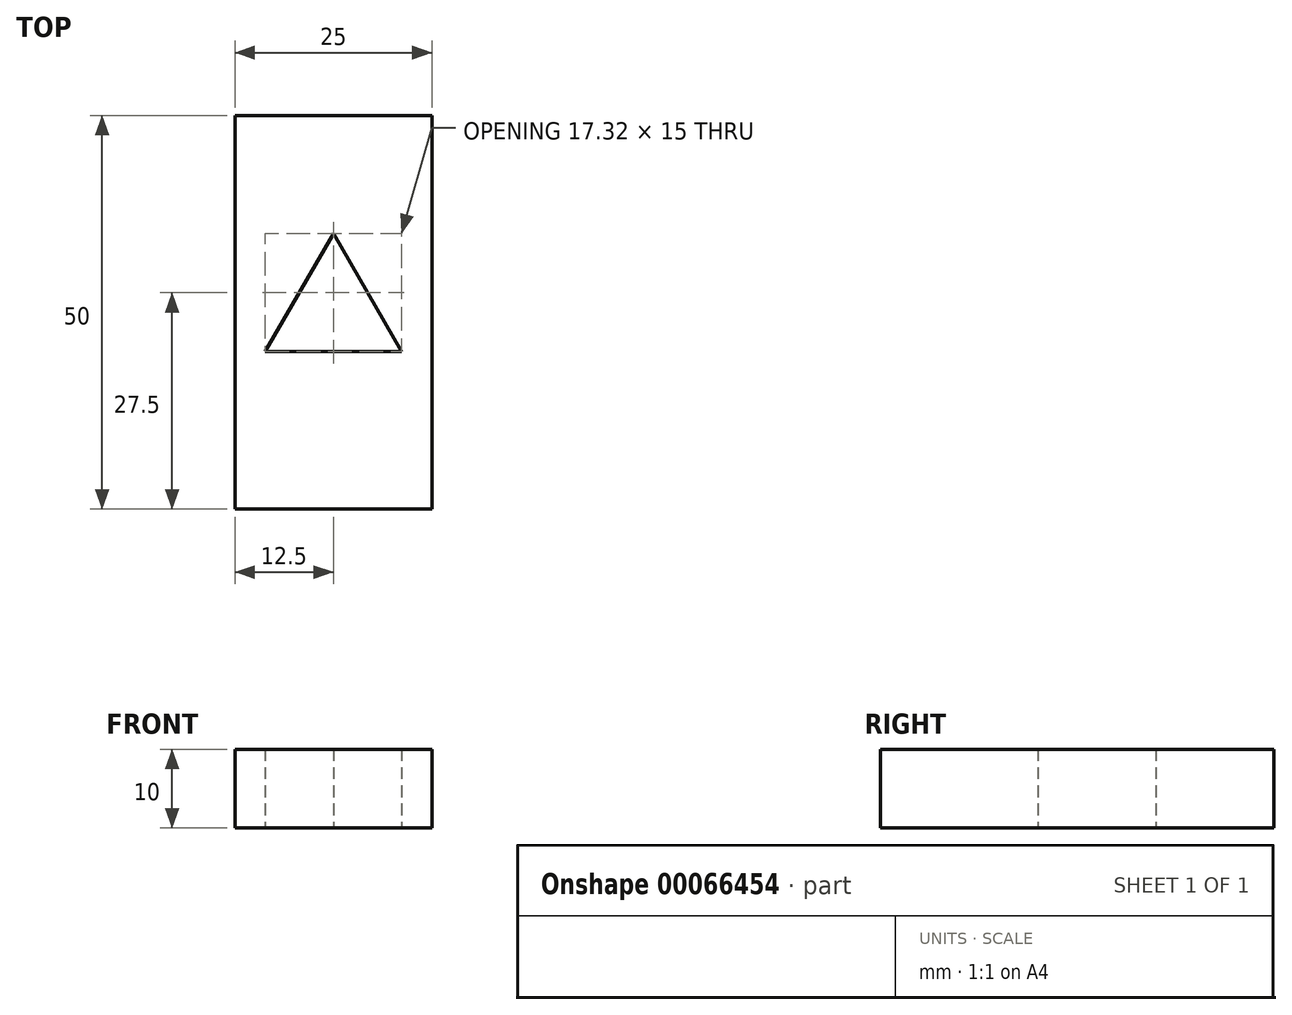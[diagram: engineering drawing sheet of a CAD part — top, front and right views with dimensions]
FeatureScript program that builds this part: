
annotation { "Feature Type Name" : "Feature", "Feature Type Description" : "" }
export const myFeature = defineFeature(function(context is Context, id is Id, definition is map)
    precondition{}
    {
        {
            var Q0;
            Q0=qCreatedBy(makeId("Top.planeOp"),FACE);
            var sketch = newSketch(context, id + "F0", { "sketchPlane" : qUnion([Q0])});
            skLineSegment(sketch, "E0.rect.bottom", {"start": v(12.5, -25) * mm, "end": v(-12.5, -25) * mm});
            skLineSegment(sketch, "E0.rect.top", {"start": v(12.5, 25) * mm, "end": v(-12.5, 25) * mm});
            skLineSegment(sketch, "E0.rect.left", {"start": v(12.5, -25) * mm, "end": v(12.5, 25) * mm});
            skLineSegment(sketch, "E0.rect.right", {"start": v(-12.5, -25) * mm, "end": v(-12.5, 25) * mm});
            skPoint(sketch, "E0.rect.middle", {"position": v(0, 0) * mm});
            skSolve(sketch);
        }
        {
            var Q0;
            Q0 = qSketchRegion(id + "F0", true);
            extrude(context, id + "F1", {"entities" : qUnion([Q0]), "depth" : 10 * mm});
        }
        {
            var Q0;
            Q0=qCreatedBy(makeId("Top.planeOp"),FACE);
            var sketch = newSketch(context, id + "F2", { "sketchPlane" : qUnion([Q0])});
            skCircle(sketch, "E1.cCircle", {"center": v(0, 0) * mm, "radius": 5 * mm, "construction": true});
            skLineSegment(sketch, "E1.0", {"start": v(-8.66, -5) * mm, "end": v(0, 10) * mm});
            skLineSegment(sketch, "E1.1", {"start": v(0, 10) * mm, "end": v(8.66, -5) * mm});
            skLineSegment(sketch, "E1.2", {"start": v(8.66, -5) * mm, "end": v(-8.66, -5) * mm});
            skPoint(sketch, "E1.0.midPoint", {"position": v(-4.33, 2.5) * mm});
            skSolve(sketch);
        }
        {
            var Q0;
            Q0=makeQuery(id+"F2.imprint","IMPRINT",FACE,{"disambiguationData":[TD([[makeQuery(id+"F2.imprint","IMPRINT",EDGE,{"derivedFrom":sQuery(id+"F2.wireOp",EDGE,"E1.0")}),-1.0]])]});
            extrude(context, id + "F3", {"entities" : qUnion([Q0]), "operationType" : NewBodyOperationType.REMOVE, "endBound" : BoundingType.THROUGH_ALL, "depth" : 25 * mm});
        }
    });
